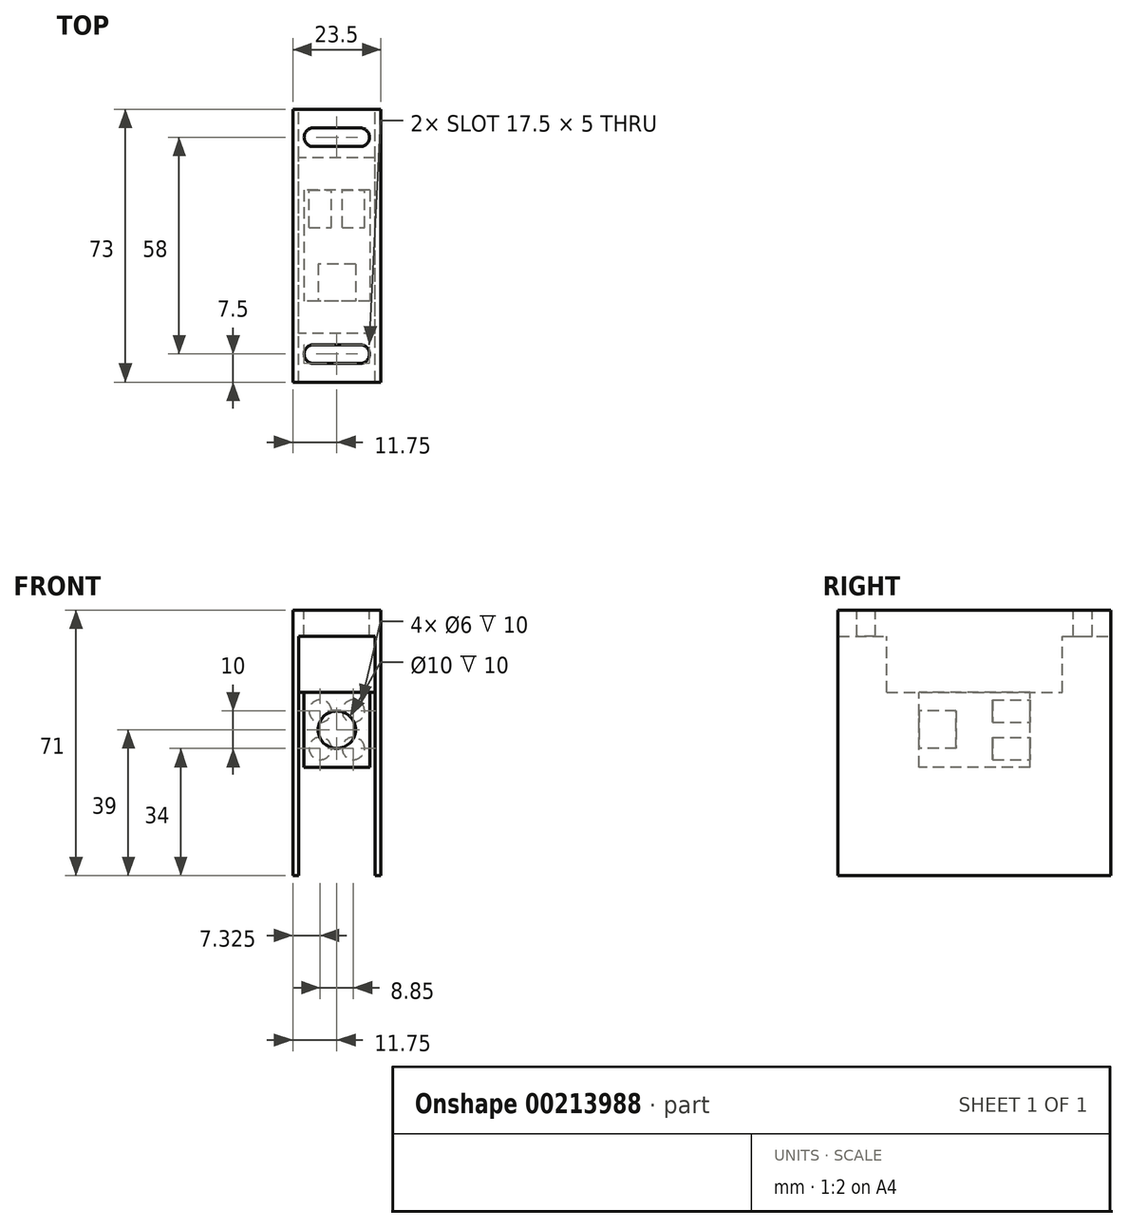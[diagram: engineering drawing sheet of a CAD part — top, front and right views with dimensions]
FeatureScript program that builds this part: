
annotation { "Feature Type Name" : "Feature", "Feature Type Description" : "" }
export const myFeature = defineFeature(function(context is Context, id is Id, definition is map)
    precondition{}
    {
        {
            var Q0;
            Q0=qCreatedBy(makeId("Top.planeOp"),FACE);
            var sketch = newSketch(context, id + "F0", { "sketchPlane" : qUnion([Q0])});
            skLineSegment(sketch, "E0.bottom", {"start": v(-11.75, 36.5) * mm, "end": v(11.75, 36.5) * mm});
            skLineSegment(sketch, "E0.top", {"start": v(-11.75, -36.5) * mm, "end": v(11.75, -36.5) * mm});
            skLineSegment(sketch, "E0.left", {"start": v(-11.75, 36.5) * mm, "end": v(-11.75, -36.5) * mm});
            skLineSegment(sketch, "E0.right", {"start": v(11.75, 36.5) * mm, "end": v(11.75, -36.5) * mm});
            skPoint(sketch, "E0.middle", {"position": v(0, 0) * mm});
            skCircle(sketch, "E1", {"center": v(6.25, 29) * mm, "radius": 2.5 * mm});
            skCircle(sketch, "E2", {"center": v(-6.25, 29) * mm, "radius": 2.5 * mm});
            skLineSegment(sketch, "E3", {"start": v(0, 36.5) * mm, "end": v(0, -36.5) * mm, "construction": true});
            skLineSegment(sketch, "E4", {"start": v(6.25, 31.5) * mm, "end": v(-6.25, 31.5) * mm});
            skLineSegment(sketch, "E5", {"start": v(-6.25, 26.5) * mm, "end": v(6.25, 26.5) * mm});
            skLineSegment(sketch, "E6", {"start": v(11.75, 0) * mm, "end": v(-11.75, 0) * mm, "construction": true});
            skLineSegment(sketch, "E7.MirrorCS", {"start": v(-6.25, -26.5) * mm, "end": v(6.25, -26.5) * mm});
            skCircle(sketch, "E8.MirrorC", {"center": v(-6.25, -29) * mm, "radius": 2.5 * mm});
            skLineSegment(sketch, "E9.MirrorCS", {"start": v(6.25, -31.5) * mm, "end": v(-6.25, -31.5) * mm});
            skCircle(sketch, "E10.MirrorC", {"center": v(6.25, -29) * mm, "radius": 2.5 * mm});
            skLineSegment(sketch, "E11", {"start": v(10.25, -36.5) * mm, "end": v(10.25, 36.5) * mm});
            skLineSegment(sketch, "E12.MirrorCS", {"start": v(-10.25, -36.5) * mm, "end": v(-10.25, 36.5) * mm});
            skLineSegment(sketch, "E13", {"start": v(10.25, 23.5) * mm, "end": v(-10.25, 23.5) * mm});
            skLineSegment(sketch, "E14.MirrorCS", {"start": v(10.25, -23.5) * mm, "end": v(-10.25, -23.5) * mm});
            skSolve(sketch);
        }
        {
            var Q0;
            {var subQ0=sQuery(id+"F0.wireOp",EDGE,"E13");Q0=makeQuery(id+"F0.imprint","IMPRINT",FACE,{"disambiguationData":[TD([[makeQuery(id+"F0.imprint","IMPRINT",EDGE,{"derivedFrom":subQ0}),1.0]])]});}
            extrude(context, id + "F1", {"entities" : qUnion([Q0]), "oppositeDirection" : true, "depth" : 22 * mm});
        }
        {
            var Q0;
            {var subQ2=sQuery(id+"F0.wireOp",EDGE,"E7.MirrorCS");Q0=makeQuery(id+"F0.imprint","IMPRINT",FACE,{"disambiguationData":[TD([[makeQuery(id+"F0.imprint","IMPRINT",EDGE,{"derivedFrom":subQ2}),1.0]])]});}
            var Q1;
            {var subQ0=sQuery(id+"F0.wireOp",EDGE,"E4");Q1=makeQuery(id+"F0.imprint","IMPRINT",FACE,{"disambiguationData":[TD([[makeQuery(id+"F0.imprint","IMPRINT",EDGE,{"derivedFrom":subQ0}),-1.0]])]});}
            extrude(context, id + "F2", {"entities" : qUnion([Q0, Q1]), "operationType" : NewBodyOperationType.ADD, "oppositeDirection" : true, "depth" : 7 * mm});
        }
        {
            var Q0;
            {var subQ0=sQuery(id+"F0.wireOp",EDGE,"E0.left");Q0=makeQuery(id+"F0.imprint","IMPRINT",FACE,{"disambiguationData":[TD([[makeQuery(id+"F0.imprint","IMPRINT",EDGE,{"derivedFrom":subQ0}),1.0]])]});}
            var Q1;
            {var subQ0=sQuery(id+"F0.wireOp",EDGE,"E0.right");Q1=makeQuery(id+"F0.imprint","IMPRINT",FACE,{"disambiguationData":[TD([[makeQuery(id+"F0.imprint","IMPRINT",EDGE,{"derivedFrom":subQ0}),-1.0]])]});}
            extrude(context, id + "F3", {"entities" : qUnion([Q0, Q1]), "operationType" : NewBodyOperationType.ADD, "oppositeDirection" : true, "depth" : 71 * mm});
        }
        {
            var Q0;
            Q0=makeQuery(id+"F1.opExtrude","CAP_FACE",FACE,{"disambiguationData":[OSD([sQuery(id+"F0.wireOp",EDGE,"E11"),sQuery(id+"F0.wireOp",EDGE,"E12.MirrorCS"),sQuery(id+"F0.wireOp",EDGE,"E13"),sQuery(id+"F0.wireOp",EDGE,"E14.MirrorCS")])],"isStart":false});
            var sketch = newSketch(context, id + "F4", { "sketchPlane" : qUnion([Q0])});
            skLineSegment(sketch, "E15.bottom", {"start": v(8.85, -14.89) * mm, "end": v(-8.85, -14.89) * mm});
            skLineSegment(sketch, "E15.top", {"start": v(8.85, 14.89) * mm, "end": v(-8.85, 14.89) * mm});
            skLineSegment(sketch, "E15.left", {"start": v(8.85, -14.89) * mm, "end": v(8.85, 14.89) * mm});
            skLineSegment(sketch, "E15.right", {"start": v(-8.85, -14.89) * mm, "end": v(-8.85, 14.89) * mm});
            skSolve(sketch);
        }
        {
            var Q0;
            Q0=makeQuery(id+"F4.imprint","IMPRINT",FACE,{"disambiguationData":[TD([[makeQuery(id+"F4.imprint","IMPRINT",EDGE,{"derivedFrom":sQuery(id+"F4.wireOp",EDGE,"E15.bottom")}),-1.0]])]});
            extrude(context, id + "F5", {"entities" : qUnion([Q0]), "operationType" : NewBodyOperationType.ADD, "depth" : 20 * mm});
        }
        {
            var Q0;
            Q0=makeQuery(id+"F5.opExtrude","SWEPT_FACE",FACE,{"disambiguationData":[OSD([sQuery(id+"F4.wireOp",EDGE,"E15.top")])]});
            var sketch = newSketch(context, id + "F6", { "sketchPlane" : qUnion([Q0])});
            skCircle(sketch, "E16", {"center": v(0, -32) * mm, "radius": 5 * mm});
            skPoint(sketch, "E16.centerSnap0", {"position": v(-8.85, -32) * mm});
            skPoint(sketch, "E16.centerSnap1", {"position": v(0, -42) * mm});
            skSolve(sketch);
        }
        {
            var Q0;
            Q0=makeQuery(id+"F6.imprint","IMPRINT",FACE,{"disambiguationData":[TD([[makeQuery(id+"F6.imprint","IMPRINT",EDGE,{"derivedFrom":sQuery(id+"F6.wireOp",EDGE,"E16")}),1.0]])]});
            extrude(context, id + "F7", {"entities" : qUnion([Q0]), "operationType" : NewBodyOperationType.REMOVE, "oppositeDirection" : true, "depth" : 10 * mm});
        }
        {
            var Q0;
            Q0=makeQuery(id+"F5.opExtrude","SWEPT_FACE",FACE,{"disambiguationData":[OSD([sQuery(id+"F4.wireOp",EDGE,"E15.bottom")])]});
            var sketch = newSketch(context, id + "F8", { "sketchPlane" : qUnion([Q0])});
            skLineSegment(sketch, "E17", {"start": v(0, -42) * mm, "end": v(0, -32) * mm, "construction": true});
            skLineSegment(sketch, "E18", {"start": v(0, -32) * mm, "end": v(0, -22) * mm, "construction": true});
            skLineSegment(sketch, "E19", {"start": v(0, -32) * mm, "end": v(8.85, -32) * mm, "construction": true});
            skLineSegment(sketch, "E20", {"start": v(0, -32) * mm, "end": v(-8.85, -32) * mm, "construction": true});
            skCircle(sketch, "E21", {"center": v(4.42, -37) * mm, "radius": 3 * mm});
            skPoint(sketch, "E21.centerSnap0", {"position": v(0, -37) * mm});
            skPoint(sketch, "E21.centerSnap1", {"position": v(4.42, -32) * mm});
            skCircle(sketch, "E22", {"center": v(-4.42, -37) * mm, "radius": 3 * mm});
            skPoint(sketch, "E22.centerSnap0", {"position": v(-4.42, -32) * mm});
            skCircle(sketch, "E23", {"center": v(-4.42, -27) * mm, "radius": 3 * mm});
            skPoint(sketch, "E23.centerSnap0", {"position": v(0, -27) * mm});
            skCircle(sketch, "E24", {"center": v(4.42, -27) * mm, "radius": 3 * mm});
            skSolve(sketch);
        }
        {
            var Q0;
            Q0=makeQuery(id+"F8.imprint","IMPRINT",FACE,{"disambiguationData":[TD([[makeQuery(id+"F8.imprint","IMPRINT",EDGE,{"derivedFrom":sQuery(id+"F8.wireOp",EDGE,"E24")}),1.0]])]});
            var Q1;
            Q1=makeQuery(id+"F8.imprint","IMPRINT",FACE,{"disambiguationData":[TD([[makeQuery(id+"F8.imprint","IMPRINT",EDGE,{"derivedFrom":sQuery(id+"F8.wireOp",EDGE,"E21")}),1.0]])]});
            var Q2;
            Q2=makeQuery(id+"F8.imprint","IMPRINT",FACE,{"disambiguationData":[TD([[makeQuery(id+"F8.imprint","IMPRINT",EDGE,{"derivedFrom":sQuery(id+"F8.wireOp",EDGE,"E22")}),1.0]])]});
            var Q3;
            Q3=makeQuery(id+"F8.imprint","IMPRINT",FACE,{"disambiguationData":[TD([[makeQuery(id+"F8.imprint","IMPRINT",EDGE,{"derivedFrom":sQuery(id+"F8.wireOp",EDGE,"E23")}),1.0]])]});
            var Q4;
            Q4=sQuery(id+"F8.wireOp",EDGE,"E22");
            extrude(context, id + "F9", {"entities" : qUnion([Q0, Q1, Q2, Q3]), "operationType" : NewBodyOperationType.REMOVE, "surfaceEntities" : qUnion([Q4]), "oppositeDirection" : true, "depth" : 10 * mm});
        }
    });
